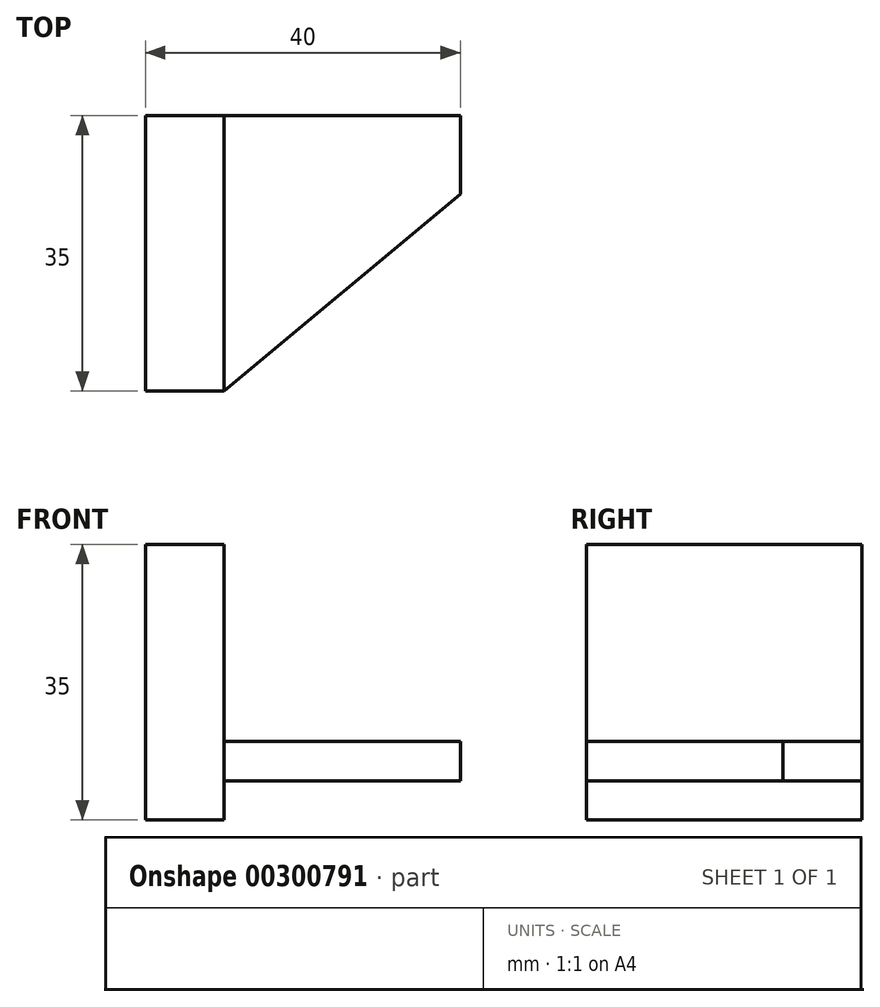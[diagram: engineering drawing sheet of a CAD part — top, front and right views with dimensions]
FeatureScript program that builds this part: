
annotation { "Feature Type Name" : "Feature", "Feature Type Description" : "" }
export const myFeature = defineFeature(function(context is Context, id is Id, definition is map)
    precondition{}
    {
        {
            var Q0;
            Q0=qCreatedBy(makeId("Front.planeOp"),FACE);
            var sketch = newSketch(context, id + "F0", { "sketchPlane" : qUnion([Q0])});
            skLineSegment(sketch, "E0.bottom", {"start": v(32.5, 20) * mm, "end": v(-32.5, 20) * mm});
            skLineSegment(sketch, "E0.top", {"start": v(32.5, -20) * mm, "end": v(-32.5, -20) * mm});
            skLineSegment(sketch, "E0.left", {"start": v(32.5, 20) * mm, "end": v(32.5, -20) * mm});
            skLineSegment(sketch, "E0.right", {"start": v(-32.5, 20) * mm, "end": v(-32.5, -20) * mm});
            skPoint(sketch, "E0.middle", {"position": v(0, 0) * mm});
            skLineSegment(sketch, "E1", {"start": v(-7.5, 20) * mm, "end": v(32.5, 0) * mm});
            skLineSegment(sketch, "E2.bottom", {"start": v(-32.5, 15) * mm, "end": v(-22.5, 15) * mm});
            skLineSegment(sketch, "E2.top", {"start": v(-32.5, -20) * mm, "end": v(-22.5, -20) * mm});
            skLineSegment(sketch, "E2.left", {"start": v(-32.5, 15) * mm, "end": v(-32.5, -20) * mm});
            skLineSegment(sketch, "E2.right", {"start": v(-22.5, 15) * mm, "end": v(-22.5, -20) * mm});
            skLineSegment(sketch, "E3.bottom", {"start": v(-22.5, -10) * mm, "end": v(7.5, -10) * mm});
            skLineSegment(sketch, "E3.top", {"start": v(-22.5, -15) * mm, "end": v(7.5, -15) * mm});
            skLineSegment(sketch, "E3.left", {"start": v(-22.5, -10) * mm, "end": v(-22.5, -15) * mm});
            skLineSegment(sketch, "E3.right", {"start": v(7.5, -10) * mm, "end": v(7.5, -15) * mm});
            skSolve(sketch);
        }
        {
            var Q0;
            {var subQ1=sQuery(id+"F0.wireOp",EDGE,"E0.top");Q0=makeQuery(id+"F0.imprint","IMPRINT",FACE,{"disambiguationData":[TD([[makeQuery(id+"F0.imprint","IMPRINT",EDGE,{"derivedFrom":subQ1}),-1.0]])]});}
            extrude(context, id + "F1", {"entities" : qUnion([Q0]), "depth" : 10 * mm});
        }
        {
            var Q0;
            {var subQ1=sQuery(id+"F0.wireOp",EDGE,"E2.bottom");Q0=makeQuery(id+"F0.imprint","IMPRINT",FACE,{"disambiguationData":[TD([[makeQuery(id+"F0.imprint","IMPRINT",EDGE,{"derivedFrom":subQ1}),-1.0]])]});}
            var Q1;
            Q1=makeQuery(id+"F0.imprint","IMPRINT",FACE,{"disambiguationData":[TD([[makeQuery(id+"F0.imprint","IMPRINT",EDGE,{"derivedFrom":sQuery(id+"F0.wireOp",EDGE,"E3.bottom")}),-1.0]])]});
            extrude(context, id + "F2", {"entities" : qUnion([Q0, Q1]), "operationType" : NewBodyOperationType.ADD, "depth" : 35 * mm});
        }
        {
            var Q0;
            Q0=makeQuery(id+"F2.opExtrude","SWEPT_FACE",FACE,{"disambiguationData":[OSD([sQuery(id+"F0.wireOp",EDGE,"E3.bottom")])]});
            var sketch = newSketch(context, id + "F3", { "sketchPlane" : qUnion([Q0])});
            skLineSegment(sketch, "E4", {"start": v(-22.5, -35) * mm, "end": v(7.5, -10) * mm});
            skSolve(sketch);
        }
        {
            var Q0;
            Q0=makeQuery(id+"F3.imprint","IMPRINT",FACE,{"disambiguationData":[TD([[makeQuery(id+"F3.imprint","IMPRINT",EDGE,{"derivedFrom":sQuery(id+"F3.wireOp",EDGE,"E4")}),-1.0]])]});
            extrude(context, id + "F4", {"entities" : qUnion([Q0]), "operationType" : NewBodyOperationType.REMOVE, "endBound" : BoundingType.THROUGH_ALL, "oppositeDirection" : true, "depth" : 25 * mm});
        }
    });
